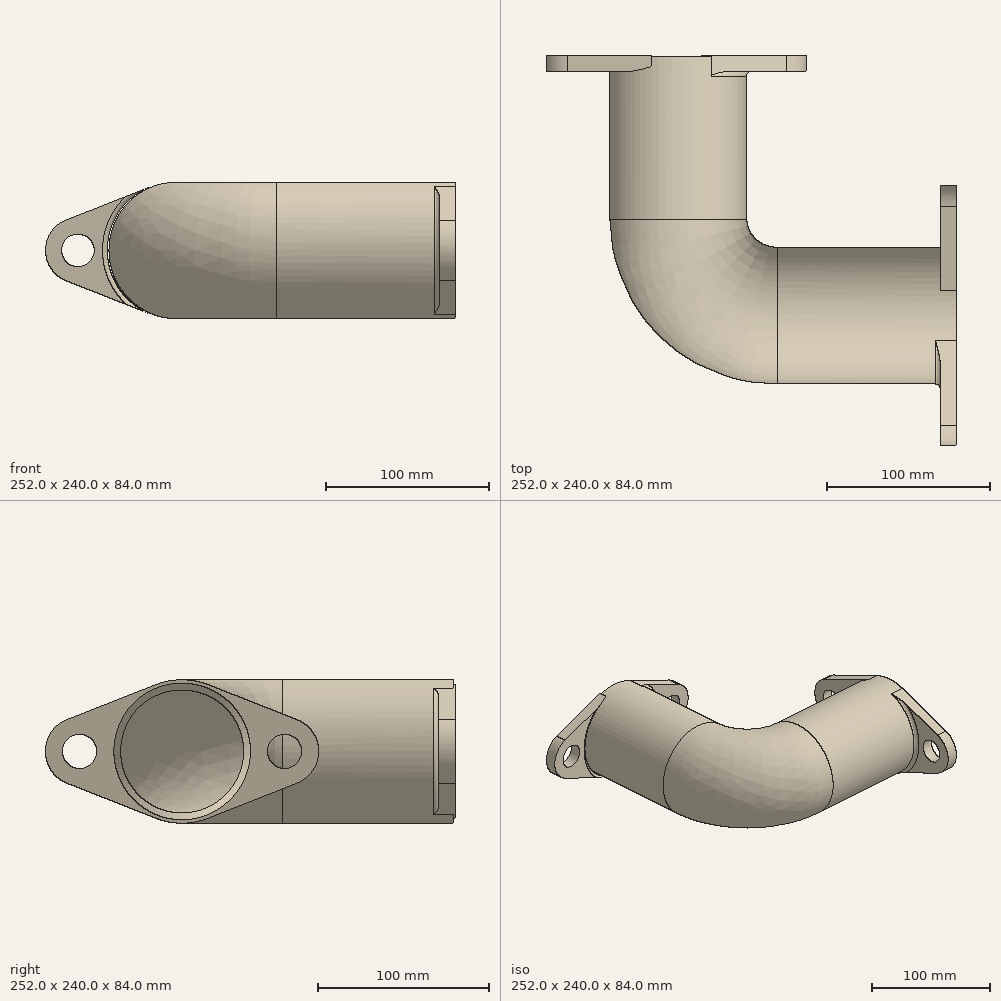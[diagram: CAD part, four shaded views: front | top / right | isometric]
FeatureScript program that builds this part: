
annotation { "Feature Type Name" : "Feature", "Feature Type Description" : "" }
export const myFeature = defineFeature(function(context is Context, id is Id, definition is map)
    precondition{}
    {
        {
            var Q0;
            Q0=qCreatedBy(makeId("Top.planeOp"),FACE);
            var sketch = newSketch(context, id + "F0", { "sketchPlane" : qUnion([Q0])});
            skLineSegment(sketch, "E0", {"start": v(0, 0) * mm, "end": v(-1, 0) * mm});
            skLineSegment(sketch, "E1", {"start": v(-1, 0) * mm, "end": v(-101, 0) * mm});
            skLineSegment(sketch, "E2", {"start": v(-161, 60) * mm, "end": v(-161, 160) * mm});
            skPoint(sketch, "E3.visualSharp", {"position": v(-161, 0) * mm});
            skArc(sketch, "E3.filletArc", {"start": v(-161, 60) * mm, "mid": v(-143.43, 17.57) * mm, "end": v(-101, 0) * mm});
            skSolve(sketch);
        }
        {
            var Q0;
            Q0=qCreatedBy(makeId("Right.planeOp"),FACE);
            var sketch = newSketch(context, id + "F1", { "sketchPlane" : qUnion([Q0])});
            skCircle(sketch, "E4", {"center": v(0, 0) * mm, "radius": 42 * mm});
            skLineSegment(sketch, "E5", {"start": v(0, 0) * mm, "end": v(-60, 0) * mm});
            skCircle(sketch, "E6", {"center": v(-60, 0) * mm, "radius": 10 * mm});
            skLineSegment(sketch, "E7", {"start": v(0, 0) * mm, "end": v(60, 0) * mm});
            skCircle(sketch, "E8", {"center": v(60, 0) * mm, "radius": 10 * mm});
            skArc(sketch, "E9", {"start": v(67.33, -18.6) * mm, "mid": v(80, 0) * mm, "end": v(67.33, 18.6) * mm});
            skCircle(sketch, "E10", {"center": v(0, 0) * mm, "radius": 36 * mm});
            skCircle(sketch, "E11", {"center": v(0, 0) * mm, "radius": 30 * mm});
            skLineSegment(sketch, "E12", {"start": v(-15.4, -39.07) * mm, "end": v(-67.33, -18.6) * mm});
            skLineSegment(sketch, "E13", {"start": v(-15.4, 39.07) * mm, "end": v(-67.33, 18.6) * mm});
            skLineSegment(sketch, "E14", {"start": v(15.4, 39.07) * mm, "end": v(67.33, 18.6) * mm});
            skLineSegment(sketch, "E15.trimOffspring", {"start": v(67.33, -18.6) * mm, "end": v(15.4, -39.07) * mm});
            skPoint(sketch, "E16.orphan", {"position": v(-114.55, 0) * mm});
            skArc(sketch, "E17.trimOffspring", {"start": v(-67.33, 18.6) * mm, "mid": v(-80, 0) * mm, "end": v(-67.33, -18.6) * mm});
            skSolve(sketch);
        }
        {
            var Q0;
            Q0=qCreatedBy(makeId("Front.planeOp"),FACE);
            cPlane(context, id + "F2", {"entities" : qUnion([Q0]), "cplaneType" : CPlaneType.OFFSET, "offset" : 160 * mm, "oppositeDirection" : true, "width" : 150 * mm, "height" : 150 * mm});
        }
        {
            var Q0;
            Q0=qCreatedBy(id+"F2.planeOp",FACE);
            var sketch = newSketch(context, id + "F3", { "sketchPlane" : qUnion([Q0])});
            skCircle(sketch, "E18", {"center": v(-162, 0) * mm, "radius": 42 * mm});
            skLineSegment(sketch, "E19", {"start": v(-162, 0) * mm, "end": v(-222, 0) * mm});
            skCircle(sketch, "E20", {"center": v(-222, 0) * mm, "radius": 10 * mm});
            skLineSegment(sketch, "E21", {"start": v(-162, 0) * mm, "end": v(-102, 0) * mm});
            skCircle(sketch, "E22", {"center": v(-102, 0) * mm, "radius": 10 * mm});
            skArc(sketch, "E23", {"start": v(-94.67, -18.6) * mm, "mid": v(-82, 0) * mm, "end": v(-94.67, 18.6) * mm});
            skCircle(sketch, "E24", {"center": v(-162, 0) * mm, "radius": 36 * mm});
            skCircle(sketch, "E25", {"center": v(-162, 0) * mm, "radius": 30 * mm});
            skLineSegment(sketch, "E26", {"start": v(-177.4, -39.07) * mm, "end": v(-229.33, -18.6) * mm});
            skLineSegment(sketch, "E27", {"start": v(-177.4, 39.07) * mm, "end": v(-229.33, 18.6) * mm});
            skLineSegment(sketch, "E28", {"start": v(-146.6, 39.07) * mm, "end": v(-94.67, 18.6) * mm});
            skLineSegment(sketch, "E29.trimOffspring", {"start": v(-94.67, -18.6) * mm, "end": v(-146.6, -39.07) * mm});
            skPoint(sketch, "E30.orphan", {"position": v(-276.55, 0) * mm});
            skArc(sketch, "E31.trimOffspring", {"start": v(-229.33, 18.6) * mm, "mid": v(-242, 0) * mm, "end": v(-229.33, -18.6) * mm});
            skSolve(sketch);
        }
        {
            var Q0;
            {var subQ1=sQuery(id+"F1.wireOp",EDGE,"E4");var subQ6=makeQuery(id+"F1.imprint","INTERSECT",VERTEX,{"derivedFrom":[subQ1,sQuery(id+"F1.wireOp",EDGE,"E15.trimOffspring")]});Q0=makeQuery(id+"F1.imprint","IMPRINT",FACE,{"disambiguationData":[TD([[makeQuery(id+"F1.imprint","IMPRINT",EDGE,{"disambiguationData":[TD([[subQ6,-1.0]])],"derivedFrom":subQ1}),1.0]])]});}
            var Q1;
            {var subQ1=sQuery(id+"F1.wireOp",EDGE,"E4");var subQ6=makeQuery(id+"F1.imprint","INTERSECT",VERTEX,{"derivedFrom":[subQ1,sQuery(id+"F1.wireOp",EDGE,"E14")]});Q1=makeQuery(id+"F1.imprint","IMPRINT",FACE,{"disambiguationData":[TD([[makeQuery(id+"F1.imprint","IMPRINT",EDGE,{"disambiguationData":[TD([[subQ6,1.0]])],"derivedFrom":subQ1}),1.0]])]});}
            var Q2;
            Q2=sQuery(id+"F0.wireOp",EDGE,"E1");
            var Q3;
            Q3=sQuery(id+"F0.wireOp",EDGE,"E3.filletArc");
            var Q4;
            Q4=sQuery(id+"F0.wireOp",EDGE,"E2");
            sweep(context, id + "F4", {"profiles" : qUnion([Q0, Q1]), "path" : qUnion([Q2, Q3, Q4])});
        }
        {
            var Q0;
            Q0 = qSketchRegion(id + "F1", true);
            extrude(context, id + "F5", {"entities" : qUnion([Q0]), "operationType" : NewBodyOperationType.ADD, "depth" : 10 * mm, "offsetDistance" : 25 * mm});
        }
        {
            var Q0;
            Q0=makeQuery(id+"F3.imprint","IMPRINT",FACE,{"disambiguationData":[TD([[makeQuery(id+"F3.imprint","IMPRINT",EDGE,{"derivedFrom":sQuery(id+"F3.wireOp",EDGE,"E22")}),-1.0]])]});
            var Q1;
            Q1=makeQuery(id+"F3.imprint","IMPRINT",FACE,{"disambiguationData":[TD([[makeQuery(id+"F3.imprint","IMPRINT",EDGE,{"derivedFrom":sQuery(id+"F3.wireOp",EDGE,"E20")}),-1.0]])]});
            extrude(context, id + "F6", {"entities" : qUnion([Q0, Q1]), "operationType" : NewBodyOperationType.ADD, "depth" : 10 * mm, "offsetDistance" : 25 * mm});
        }
        {
            var Q0;
            {var subQ0=sQuery(id+"F3.wireOp",EDGE,"E18");Q0=makeQuery(id+"F6.opExtrude","CAP_EDGE",EDGE,{"disambiguationData":[OSD([subQ0]),TDD([makeQuery(id+"F3.imprint","IMPRINT",EDGE,{"disambiguationData":[TD([[makeQuery(id+"F3.imprint","INTERSECT",VERTEX,{"derivedFrom":[subQ0,sQuery(id+"F3.wireOp",EDGE,"E27")]}),-1.0]])],"derivedFrom":subQ0}),makeQuery(id+"F3.imprint","IMPRINT",EDGE,{"disambiguationData":[TD([[makeQuery(id+"F3.imprint","INTERSECT",VERTEX,{"derivedFrom":[subQ0,sQuery(id+"F3.wireOp",EDGE,"E26")]}),1.0]])],"derivedFrom":subQ0})])],"isStart":false});}
            var Q1;
            Q1=makeQuery(id+"F6.boolean.opBoolean","INTERSECT",EDGE,{"derivedFrom":[makeQuery(id+"F4.opSweep","SWEPT_FACE",FACE,{"disambiguationData":[OSD([sQuery(id+"F0.wireOp",EDGE,"E2"),sQuery(id+"F1.wireOp",EDGE,"E4")])]}),makeQuery(id+"F6.opExtrude","CAP_FACE",FACE,{"disambiguationData":[OSD([sQuery(id+"F3.wireOp",EDGE,"E18"),sQuery(id+"F3.wireOp",EDGE,"E22"),sQuery(id+"F3.wireOp",EDGE,"E23"),sQuery(id+"F3.wireOp",EDGE,"E28"),sQuery(id+"F3.wireOp",EDGE,"E29.trimOffspring")])],"isStart":false})]});
            var Q2;
            {var subQ0=sQuery(id+"F1.wireOp",EDGE,"E12");var subQ1=sQuery(id+"F1.wireOp",EDGE,"E4");Q2=makeQuery(id+"F5.boolean.opBoolean","SPLIT",EDGE,{"disambiguationData":[TD([makeQuery(id+"F5.opExtrude","SWEPT_FACE",FACE,{"disambiguationData":[OSD([subQ0])]})])],"derivedFrom":makeQuery(id+"F4.opSweep","CAP_EDGE",EDGE,{"disambiguationData":[OSD([sQuery(id+"F0.wireOp",VERTEX,"E1.start"),subQ1])],"isStart":true})});}
            var Q3;
            {var subQ1=sQuery(id+"F1.wireOp",EDGE,"E4");var subQ4=sQuery(id+"F1.wireOp",EDGE,"E14");Q3=makeQuery(id+"F5.boolean.opBoolean","SPLIT",EDGE,{"disambiguationData":[TD([makeQuery(id+"F5.opExtrude","SWEPT_FACE",FACE,{"disambiguationData":[OSD([subQ4])]})])],"derivedFrom":makeQuery(id+"F4.opSweep","CAP_EDGE",EDGE,{"disambiguationData":[OSD([sQuery(id+"F0.wireOp",VERTEX,"E1.start"),subQ1])],"isStart":true})});}
            fillet(context, id + "F7", {"entities" : qUnion([Q0, Q1, Q2, Q3]), "radius" : 3 * mm, "tangentPropagation" : true, "allowEdgeOverflow" : false});
        }
        {
            var Q0;
            Q0=makeQuery(id+"F5.opExtrude","CAP_EDGE",EDGE,{"disambiguationData":[OSD([sQuery(id+"F1.wireOp",EDGE,"E10")])],"isStart":false});
            var Q1;
            Q1=makeQuery(id+"F4.opSweep","CAP_EDGE",EDGE,{"disambiguationData":[OSD([sQuery(id+"F0.wireOp",VERTEX,"E2.end"),sQuery(id+"F1.wireOp",EDGE,"E10")])],"isStart":false});
            chamfer(context, id + "F8", {"entities" : qUnion([Q0, Q1]), "width" : 4 * mm, "tangentPropagation" : true});
        }
    });
